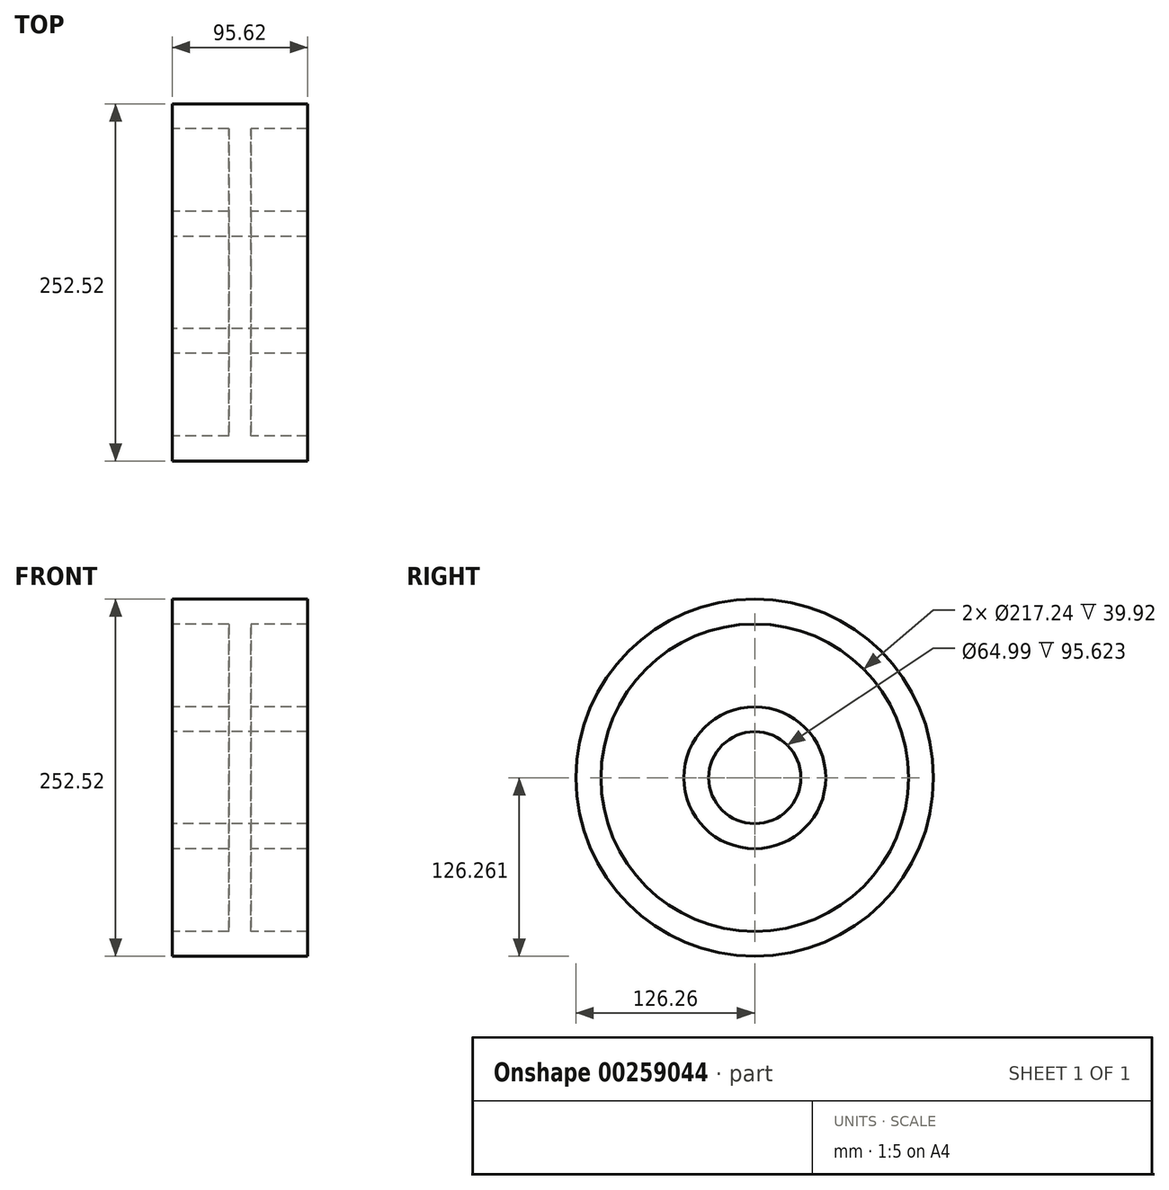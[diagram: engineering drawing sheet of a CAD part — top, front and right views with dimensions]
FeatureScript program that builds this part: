
annotation { "Feature Type Name" : "Feature", "Feature Type Description" : "" }
export const myFeature = defineFeature(function(context is Context, id is Id, definition is map)
    precondition{}
    {
        {
            var Q0;
            Q0=qCreatedBy(makeId("Front.planeOp"),FACE);
            var sketch = newSketch(context, id + "F0", { "sketchPlane" : qUnion([Q0])});
            skLineSegment(sketch, "E0", {"start": v(-47.81, 51.06) * mm, "end": v(47.81, 51.06) * mm});
            skLineSegment(sketch, "E1", {"start": v(47.81, 51.06) * mm, "end": v(47.81, 33.42) * mm});
            skLineSegment(sketch, "E2", {"start": v(47.81, 33.42) * mm, "end": v(7.9, 33.42) * mm});
            skLineSegment(sketch, "E3", {"start": v(7.9, 33.42) * mm, "end": v(7.9, -25.07) * mm});
            skLineSegment(sketch, "E4", {"start": v(7.9, -25.07) * mm, "end": v(47.81, -25.07) * mm});
            skLineSegment(sketch, "E5", {"start": v(47.81, -25.07) * mm, "end": v(47.81, -42.7) * mm});
            skLineSegment(sketch, "E6", {"start": v(47.81, -42.7) * mm, "end": v(-47.81, -42.7) * mm});
            skLineSegment(sketch, "E7", {"start": v(-47.81, -42.7) * mm, "end": v(-47.81, -25.07) * mm});
            skLineSegment(sketch, "E8", {"start": v(-47.81, -25.07) * mm, "end": v(-7.9, -25.07) * mm});
            skLineSegment(sketch, "E9", {"start": v(-7.9, -25.07) * mm, "end": v(-7.9, 33.42) * mm});
            skLineSegment(sketch, "E10", {"start": v(-7.9, 33.42) * mm, "end": v(-47.81, 33.42) * mm});
            skLineSegment(sketch, "E11", {"start": v(-47.81, 33.42) * mm, "end": v(-47.81, 51.06) * mm});
            skLineSegment(sketch, "E12", {"start": v(0, 76.6) * mm, "end": v(0, -75.2) * mm, "construction": true});
            skLineSegment(sketch, "E13", {"start": v(-77.75, -75.2) * mm, "end": v(78.22, -75.2) * mm, "construction": true});
            skSolve(sketch);
        }
        {
            var Q0;
            Q0 = qSketchRegion(id + "F0", true);
            var Q1;
            Q1=sQuery(id+"F0.wireOp",EDGE,"E13");
            revolve(context, id + "F1", {"entities" : qUnion([Q0]), "axis" : qUnion([Q1]), "revolveType" : RevolveType.FULL});
        }
    });
